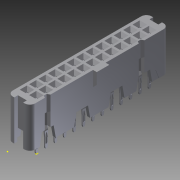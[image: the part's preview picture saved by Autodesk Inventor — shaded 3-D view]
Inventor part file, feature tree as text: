
AUTODESK INVENTOR PART (.ipt)
format: ipt  version: 2014 (Build 180170000, 170)  size: 1,916,416 bytes
history: native  units: mm
features: other x3, sketch x1, projected_geometry x1
ambient origin geometry x8: Origin, YZ Plane, XZ Plane, XY Plane, X Axis, Y Axis, Z Axis, Center Point
bodies: Volumenkörper1 (feature_tree)
feature tree (5):
  other  "8526-4500pl-01"
  sketch  "Skizze1"
  other  "Arbeitspunkt1"
  other  "Arbeitspunkt2"
  projected_geometry  "Projizierte Kontur1"
